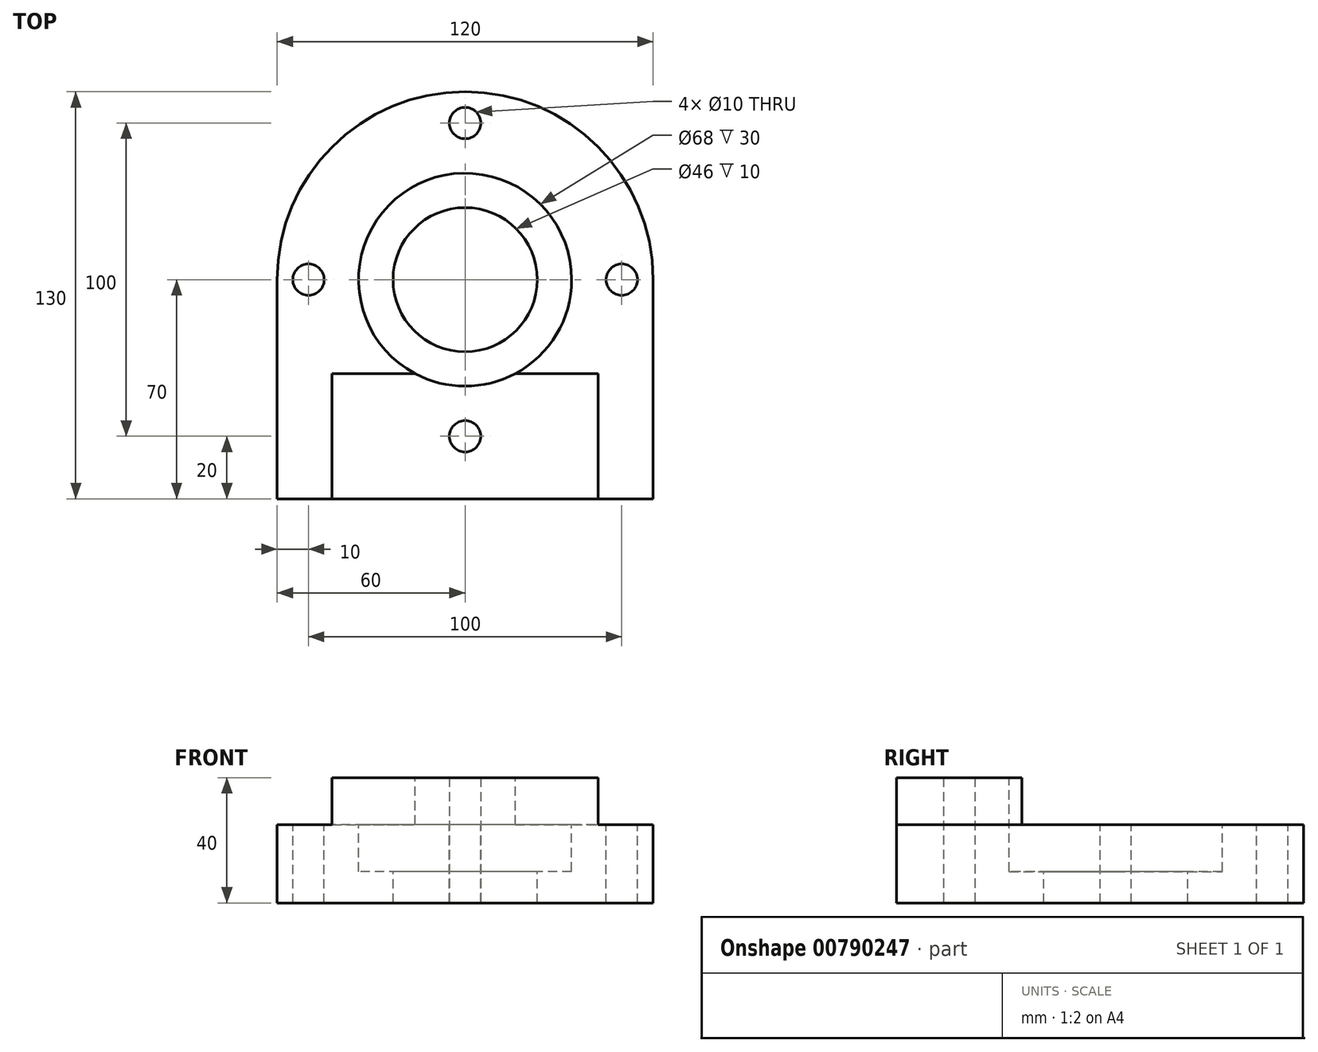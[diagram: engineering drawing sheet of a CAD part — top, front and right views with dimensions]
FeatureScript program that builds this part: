
annotation { "Feature Type Name" : "Feature", "Feature Type Description" : "" }
export const myFeature = defineFeature(function(context is Context, id is Id, definition is map)
    precondition{}
    {
        {
            var Q0;
            Q0=qCreatedBy(makeId("Top.planeOp"),FACE);
            var sketch = newSketch(context, id + "F0", { "sketchPlane" : qUnion([Q0])});
            skCircle(sketch, "E0", {"center": v(0, 0) * mm, "radius": 60 * mm});
            skLineSegment(sketch, "E1.bottom", {"start": v(-60, 0) * mm, "end": v(60, 0) * mm});
            skLineSegment(sketch, "E1.top", {"start": v(-60, -70) * mm, "end": v(60, -70) * mm});
            skLineSegment(sketch, "E1.left", {"start": v(-60, 0) * mm, "end": v(-60, -70) * mm});
            skLineSegment(sketch, "E1.right", {"start": v(60, 0) * mm, "end": v(60, -70) * mm});
            skSolve(sketch);
        }
        {
            var Q0;
            Q0=makeQuery(id+"F0.imprint","IMPRINT",FACE,{"disambiguationData":[TD([[makeQuery(id+"F0.imprint","IMPRINT",EDGE,{"derivedFrom":sQuery(id+"F0.wireOp",EDGE,"E1.top")}),1.0]])]});
            var Q1;
            {var subQ0=sQuery(id+"F0.wireOp",EDGE,"E1.bottom");Q1=makeQuery(id+"F0.imprint","IMPRINT",FACE,{"disambiguationData":[TD([[makeQuery(id+"F0.imprint","IMPRINT",EDGE,{"derivedFrom":subQ0}),-1.0]])]});}
            var Q2;
            {var subQ0=sQuery(id+"F0.wireOp",EDGE,"E1.bottom");Q2=makeQuery(id+"F0.imprint","IMPRINT",FACE,{"disambiguationData":[TD([[makeQuery(id+"F0.imprint","IMPRINT",EDGE,{"derivedFrom":subQ0}),1.0]])]});}
            extrude(context, id + "F1", {"entities" : qUnion([Q0, Q1, Q2]), "oppositeDirection" : true, "depth" : 25 * mm, "offsetDistance" : 25 * mm});
        }
        {
            var Q0;
            Q0=qCreatedBy(makeId("Top.planeOp"),FACE);
            var sketch = newSketch(context, id + "F2", { "sketchPlane" : qUnion([Q0])});
            skLineSegment(sketch, "E2.bottom", {"start": v(-42.5, -30) * mm, "end": v(42.5, -30) * mm});
            skLineSegment(sketch, "E2.top", {"start": v(-42.5, -70) * mm, "end": v(42.5, -70) * mm});
            skLineSegment(sketch, "E2.left", {"start": v(-42.5, -30) * mm, "end": v(-42.5, -70) * mm});
            skLineSegment(sketch, "E2.right", {"start": v(42.5, -30) * mm, "end": v(42.5, -70) * mm});
            skSolve(sketch);
        }
        {
            var Q0;
            Q0 = qSketchRegion(id + "F2", true);
            extrude(context, id + "F3", {"entities" : qUnion([Q0]), "operationType" : NewBodyOperationType.ADD, "depth" : 15 * mm, "offsetDistance" : 25 * mm});
        }
        {
            var Q0;
            Q0=qCreatedBy(makeId("Top.planeOp"),FACE);
            var sketch = newSketch(context, id + "F4", { "sketchPlane" : qUnion([Q0])});
            skCircle(sketch, "E3", {"center": v(0, -50) * mm, "radius": 5 * mm});
            skSolve(sketch);
        }
        {
            var Q0;
            Q0 = qSketchRegion(id + "F4", true);
            extrude(context, id + "F5", {"entities" : qUnion([Q0]), "operationType" : NewBodyOperationType.REMOVE, "depth" : 15 * mm, "offsetDistance" : 25 * mm, "hasSecondDirection" : true, "secondDirectionOppositeDirection" : true, "secondDirectionDepth" : 25 * mm});
        }
        {
            var Q0;
            Q0=qCreatedBy(makeId("Top.planeOp"),FACE);
            var sketch = newSketch(context, id + "F6", { "sketchPlane" : qUnion([Q0])});
            skCircle(sketch, "E4", {"center": v(0, 0) * mm, "radius": 34 * mm});
            skSolve(sketch);
        }
        {
            var Q0;
            Q0 = qSketchRegion(id + "F6", true);
            extrude(context, id + "F7", {"entities" : qUnion([Q0]), "operationType" : NewBodyOperationType.REMOVE, "oppositeDirection" : true, "depth" : 15 * mm, "offsetDistance" : 25 * mm, "hasSecondDirection" : true, "secondDirectionOppositeDirection" : false, "secondDirectionDepth" : 15 * mm});
        }
        {
            var Q0;
            Q0=qCreatedBy(makeId("Top.planeOp"),FACE);
            var sketch = newSketch(context, id + "F8", { "sketchPlane" : qUnion([Q0])});
            skCircle(sketch, "E5", {"center": v(0, 0) * mm, "radius": 23 * mm});
            skSolve(sketch);
        }
        {
            var Q0;
            Q0 = qSketchRegion(id + "F8", true);
            extrude(context, id + "F9", {"entities" : qUnion([Q0]), "operationType" : NewBodyOperationType.REMOVE, "oppositeDirection" : true, "depth" : 25 * mm, "offsetDistance" : 25 * mm});
        }
        {
            var Q0;
            Q0=qCreatedBy(makeId("Top.planeOp"),FACE);
            var sketch = newSketch(context, id + "F10", { "sketchPlane" : qUnion([Q0])});
            skCircle(sketch, "E6", {"center": v(-50, 0) * mm, "radius": 5 * mm});
            skCircle(sketch, "E7", {"center": v(0, 50) * mm, "radius": 5 * mm});
            skCircle(sketch, "E8", {"center": v(50, 0) * mm, "radius": 5 * mm});
            skSolve(sketch);
        }
        {
            var Q0;
            Q0 = qSketchRegion(id + "F10", true);
            extrude(context, id + "F11", {"entities" : qUnion([Q0]), "operationType" : NewBodyOperationType.REMOVE, "oppositeDirection" : true, "depth" : 25 * mm, "offsetDistance" : 25 * mm});
        }
    });
